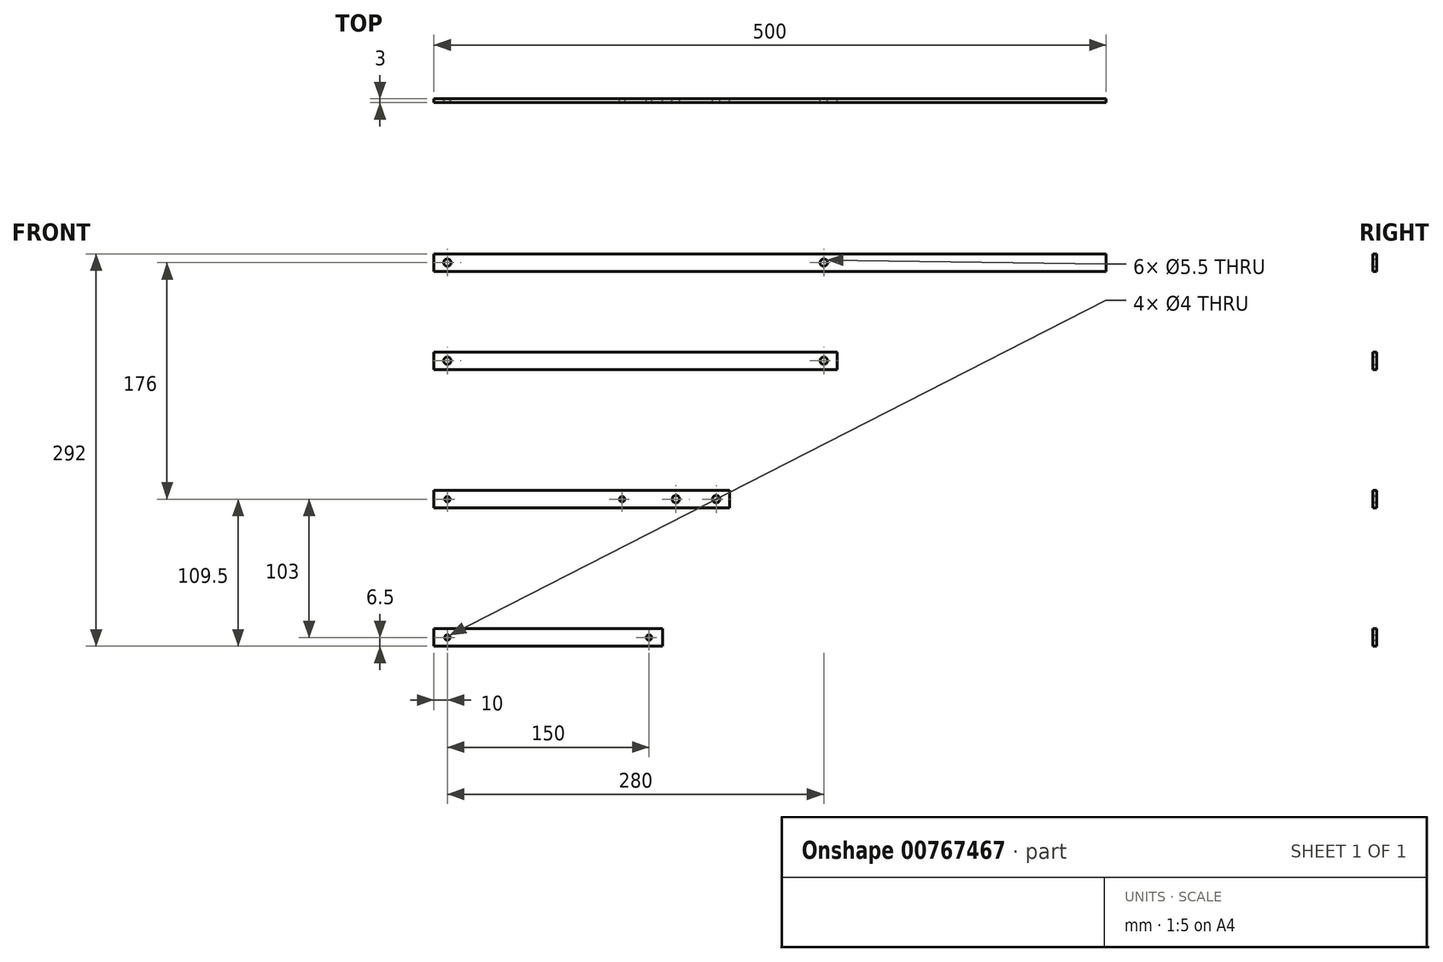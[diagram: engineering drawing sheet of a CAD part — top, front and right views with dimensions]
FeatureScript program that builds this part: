
annotation { "Feature Type Name" : "Feature", "Feature Type Description" : "" }
export const myFeature = defineFeature(function(context is Context, id is Id, definition is map)
    precondition{}
    {
        {
            var Q0;
            Q0=qCreatedBy(makeId("Front.planeOp"),FACE);
            var sketch = newSketch(context, id + "F0", { "sketchPlane" : qUnion([Q0])});
            skLineSegment(sketch, "E0.bottom", {"start": v(-180, 179.75) * mm, "end": v(320, 179.75) * mm});
            skLineSegment(sketch, "E0.top", {"start": v(-180, 166.75) * mm, "end": v(320, 166.75) * mm});
            skLineSegment(sketch, "E0.left", {"start": v(-180, 179.75) * mm, "end": v(-180, 166.75) * mm});
            skLineSegment(sketch, "E0.right", {"start": v(320, 179.75) * mm, "end": v(320, 166.75) * mm});
            skLineSegment(sketch, "E1.bottom", {"start": v(-180, 106.75) * mm, "end": v(120, 106.75) * mm});
            skLineSegment(sketch, "E1.top", {"start": v(-180, 93.75) * mm, "end": v(120, 93.75) * mm});
            skLineSegment(sketch, "E1.left", {"start": v(-180, 106.75) * mm, "end": v(-180, 93.75) * mm});
            skLineSegment(sketch, "E1.right", {"start": v(120, 106.75) * mm, "end": v(120, 93.75) * mm});
            skLineSegment(sketch, "E2.bottom", {"start": v(-180, 3.75) * mm, "end": v(40, 3.75) * mm});
            skLineSegment(sketch, "E2.top", {"start": v(-180, -9.25) * mm, "end": v(40, -9.25) * mm});
            skLineSegment(sketch, "E2.left", {"start": v(-180, 3.75) * mm, "end": v(-180, -9.25) * mm});
            skLineSegment(sketch, "E2.right", {"start": v(40, 3.75) * mm, "end": v(40, -9.25) * mm});
            skLineSegment(sketch, "E3.bottom", {"start": v(-180, -99.25) * mm, "end": v(-10, -99.25) * mm});
            skLineSegment(sketch, "E3.top", {"start": v(-180, -112.25) * mm, "end": v(-10, -112.25) * mm});
            skLineSegment(sketch, "E3.left", {"start": v(-180, -99.25) * mm, "end": v(-180, -112.25) * mm});
            skLineSegment(sketch, "E3.right", {"start": v(-10, -99.25) * mm, "end": v(-10, -112.25) * mm});
            skPoint(sketch, "E4.orphan", {"position": v(-180, -172.25) * mm});
            skLineSegment(sketch, "E5", {"start": v(-180, 173.25) * mm, "end": v(320, 173.25) * mm});
            skLineSegment(sketch, "E6", {"start": v(-180, 100.25) * mm, "end": v(120, 100.25) * mm});
            skLineSegment(sketch, "E7", {"start": v(-180, -2.75) * mm, "end": v(40, -2.75) * mm});
            skLineSegment(sketch, "E8", {"start": v(-180, -105.75) * mm, "end": v(-10, -105.75) * mm});
            skCircle(sketch, "E9", {"center": v(-170, -105.75) * mm, "radius": 2 * mm});
            skCircle(sketch, "E10", {"center": v(-20, -105.75) * mm, "radius": 2 * mm});
            skCircle(sketch, "E11", {"center": v(-170, -2.75) * mm, "radius": 2 * mm});
            skCircle(sketch, "E12", {"center": v(0, -2.75) * mm, "radius": 2.75 * mm});
            skCircle(sketch, "E13", {"center": v(-40, -2.75) * mm, "radius": 2 * mm});
            skCircle(sketch, "E14", {"center": v(-170, 100.25) * mm, "radius": 2.75 * mm});
            skCircle(sketch, "E15", {"center": v(110, 100.25) * mm, "radius": 2.75 * mm});
            skCircle(sketch, "E16", {"center": v(-170, 173.25) * mm, "radius": 2.75 * mm});
            skCircle(sketch, "E17", {"center": v(110, 173.25) * mm, "radius": 2.75 * mm});
            skCircle(sketch, "E18", {"center": v(30, -2.75) * mm, "radius": 2.75 * mm});
            skSolve(sketch);
        }
        {
            var Q0;
            Q0 = qSketchRegion(id + "F0", true);
            extrude(context, id + "F1", {"entities" : qUnion([Q0]), "depth" : 3 * mm, "offsetDistance" : 25 * mm});
        }
    });
